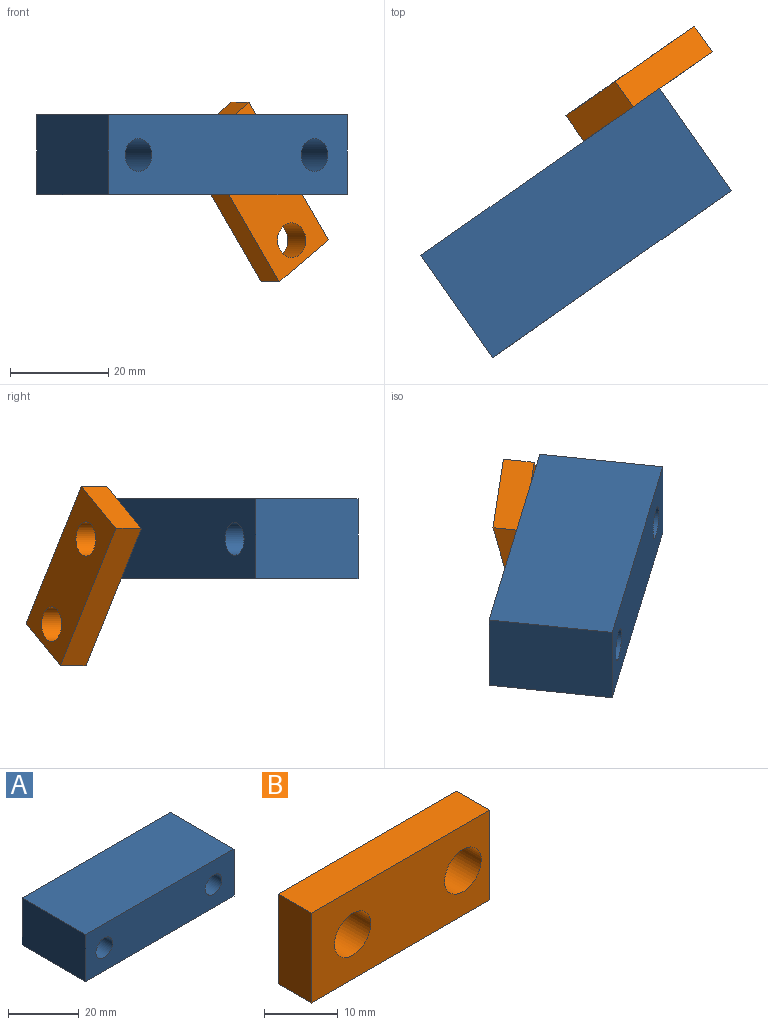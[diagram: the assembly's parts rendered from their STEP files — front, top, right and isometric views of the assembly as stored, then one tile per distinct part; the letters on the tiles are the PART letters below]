
ASSEMBLY  parts=2 mates=1
PART A: 8 faces, bbox 59.3x25.4x16.3 mm
  f0: plane 59.27x25.4mm, normal (0,0,1), area 1505.4mm2, adj f1,f5,f6,f7
  f1: plane 25.4x16.25mm, normal (-1,0,0), area 412.8mm2, adj f0,f2,f6,f7
  f2: plane 59.27x25.4mm, normal (0,0,-1), area 1505.4mm2, adj f1,f5,f6,f7
  f3: cylinder r=3.34mm len=25.4mm, axis (0,1,0), area 532.9mm2, adj f6,f7
  f4: cylinder r=3.33mm len=25.4mm, axis (0,1,0), area 531.3mm2, adj f6,f7
  f5: plane 25.4x16.25mm, normal (1,0,0), area 412.8mm2, adj f0,f2,f6,f7
  f6: plane 59.27x16.25mm, normal (0,-1,0), area 893.3mm2, adj f0,f1,f2,f3,f4,f5
  f7: plane 59.27x16.25mm, normal (0,1,0), area 893.3mm2, adj f0,f1,f2,f3,f4,f5
PART B: 8 faces, bbox 34.2x6.4x14.9 mm
  f0: plane 34.22x6.35mm, normal (0,0,1), area 217.3mm2, adj f1,f5,f6,f7
  f1: plane 14.91x6.35mm, normal (-1,0,0), area 94.7mm2, adj f0,f2,f6,f7
  f2: plane 34.22x6.35mm, normal (0,0,-1), area 217.3mm2, adj f1,f5,f6,f7
  f3: cylinder r=3.48mm len=6.96mm, axis (0,1,0), area 138.8mm2, adj f6,f7
  f4: cylinder r=3.51mm len=7.03mm, axis (0,1,0), area 140.2mm2, adj f6,f7
  f5: plane 14.91x6.35mm, normal (1,0,0), area 94.7mm2, adj f0,f2,f6,f7
  f6: plane 34.22x14.91mm, normal (0,-1,0), area 433.5mm2, adj f0,f1,f2,f3,f4,f5
  f7: plane 34.22x14.91mm, normal (0,1,0), area 433.5mm2, adj f0,f1,f2,f3,f4,f5
PLACE A rot(axis=(0,0,1),35deg) t=(15.43,-16.26,-23.62)mm
PLACE B rot(axis=(-0.26,0.83,0.5),64.5deg) t=(2.55,-17.52,4.81)mm
MATE revolute A.f4 <-> B.f3  axis (-0.57,0.82,0) through (15.43,-16.26,12.71)mm
